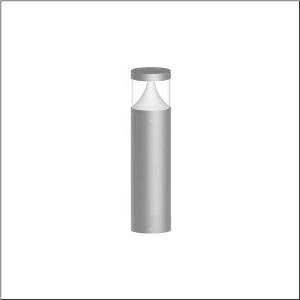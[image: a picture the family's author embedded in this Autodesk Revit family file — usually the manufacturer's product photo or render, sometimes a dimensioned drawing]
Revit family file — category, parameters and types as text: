
# Revit family: cl_31_poller_60_5cl434603
name_source: partatom
category: Lighting Fixtures
units: mm (PartAtom-declared; Revit-internal decimal feet)

## family parameters
Cut with Voids When Loaded = No
Host = Face
Light Source = No
Part Type = Normal
Room Calculation Point = No
Round Connector Dimension = Use Diameter
Shared = No

## types (1)
- --- (1 x LED, 1500 lm, 14 W, 3000K)
    Apparent Load = 14 VA
    CIE Flux Codes = 19 66 88 92 100
    Color Rendering = 80
    Color Temperature = 3000K
    Default Elevation = 1800 mm
    Description = CL 31 Bollard 60, bollard luminaire, primary light control with lens, of PC, primary optical cover: cover panel, of PC, transparent, secondary light control with reflector, of PC, primary light characteristic: asymmetric, LED, rated luminous flux: 1.500lm, luminous efficacy: 107lm/W, light colour: 830, colour temperature: 3000K, control gear: DALI, with terminal, 5-pole, max. 2.5mm², mains connection: 220..240V, AC, 50/60Hz, rated input power: 14W, luminaire housing, of aluminium, powder-coated, Siteco® metallic grey, diameter: 170mm, height: 600mm, protection rating (complete): IP65, insulation class (complete): insulation class I (protective earthing), certification: CE, ENEC, impact resistance: IK10, permissible operating ambient temperature for outdoor applications: -20..+50°C, packaging unit: 1 piece
    Height = 200 mm  [stored 0.656168 ft]
    Lamp = 1 x LED
    Lamp Light Flux = 1500 lm
    Lamp Power = 14 W
    Lamp count = 1
    Length = 170 mm  [stored 0.557743 ft]
    Luminous efficacy = 107 lm/W
    Manufacturer = Siteco
    ModVariant = No
    Model = 5CL434603
    Mounting Place = Floor
    Mounting Type = Freestanding
    Number of Poles = 1
    OnlyDefault = Yes
    Power Factor = 1
    Product Name = CL 31 Poller 60
    Product group = bollard luminaire
    ProductGroupID = 1304
    Protection Class = Protection class I
    Protection Degree = IP 65
    RLX_Detail_Level = 1
    RLX_Emergency_Light_Flux = 0 lm
    RLX_Emergency_Type = 0
    RLX_Emergency_Type_DB = No
    RlxData = <blob elided: 63793 chars, md5=7565d0b8>
    Socket = socket
    Standby Power = 0 W
    System Light Flux = 1500 lm
    System Power = 14 W
    Type Comments = factory setting: luminous flux: 100 % | dim-lin: 254 | 350 mA
    Type Image = l_1006903.jpg
    URL = http://relux.com
    VarID = @adj_195272
    Voltage = 0 V
    Weight = 0.00 kg
    Width = 0 mm  [stored 0 ft]

note: [stored X ft] marks values corroborated as IEEE doubles in the binary element streams (Revit-internal decimal feet)

## geometry (parser evidence)
native form markers: Blend x4, Sweep x12
no freeform markers — native parametric forms only
